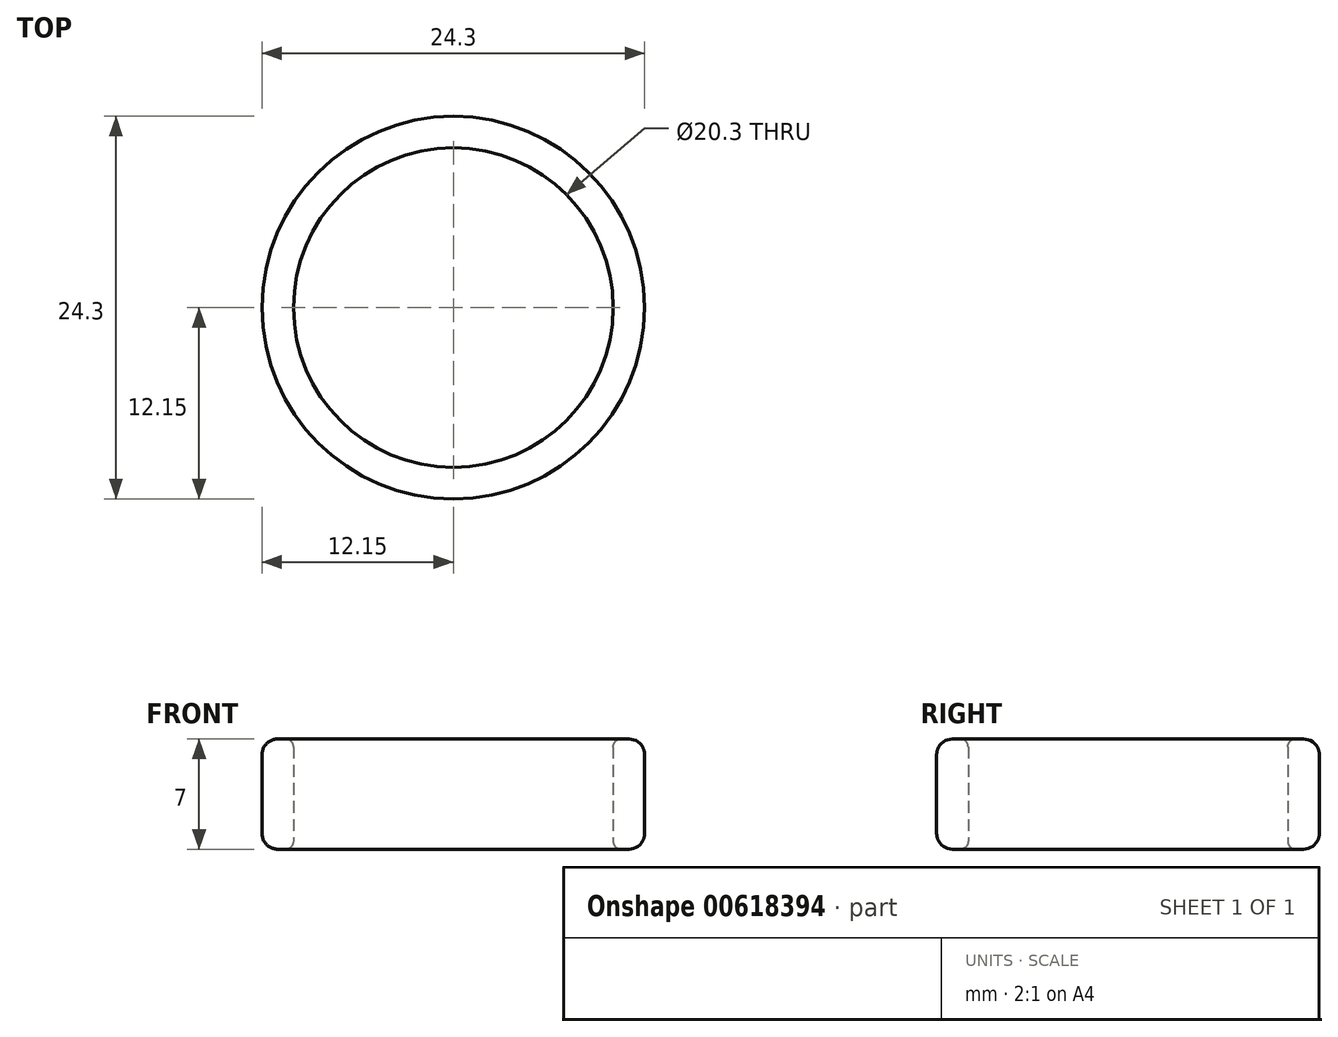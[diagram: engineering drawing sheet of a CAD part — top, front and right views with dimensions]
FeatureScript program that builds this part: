
annotation { "Feature Type Name" : "Feature", "Feature Type Description" : "" }
export const myFeature = defineFeature(function(context is Context, id is Id, definition is map)
    precondition{}
    {
        {
            var Q0;
            Q0=qCreatedBy(makeId("Front.planeOp"),FACE);
            var sketch = newSketch(context, id + "F0", { "sketchPlane" : qUnion([Q0])});
            skLineSegment(sketch, "E0", {"start": v(0, 0) * mm, "end": v(10.15, 0) * mm, "construction": true});
            skLineSegment(sketch, "E1.top", {"start": v(10.65, 3.5) * mm, "end": v(11.15, 3.5) * mm});
            skLineSegment(sketch, "E1.left", {"start": v(10.15, 0) * mm, "end": v(10.15, 3) * mm});
            skLineSegment(sketch, "E1.right", {"start": v(12.15, 0) * mm, "end": v(12.15, 2.5) * mm});
            skPoint(sketch, "E2.visualSharp", {"position": v(12.15, 3.5) * mm});
            skArc(sketch, "E2.filletArc", {"start": v(12.15, 2.5) * mm, "mid": v(11.86, 3.2) * mm, "end": v(11.15, 3.5) * mm});
            skPoint(sketch, "E3.visualSharp", {"position": v(10.15, 3.5) * mm});
            skArc(sketch, "E3.filletArc", {"start": v(10.65, 3.5) * mm, "mid": v(10.3, 3.35) * mm, "end": v(10.15, 3) * mm});
            skLineSegment(sketch, "E4.MirrorCS", {"start": v(10.65, -3.5) * mm, "end": v(11.15, -3.5) * mm});
            skArc(sketch, "E5.MirrorCS", {"start": v(10.65, -3.5) * mm, "mid": v(10.3, -3.35) * mm, "end": v(10.15, -3) * mm});
            skPoint(sketch, "E6.MirrorP", {"position": v(12.15, -3.5) * mm});
            skLineSegment(sketch, "E7.MirrorCS", {"start": v(10.15, 0) * mm, "end": v(10.15, -3) * mm});
            skArc(sketch, "E8.MirrorCS", {"start": v(12.15, -2.5) * mm, "mid": v(11.86, -3.2) * mm, "end": v(11.15, -3.5) * mm});
            skPoint(sketch, "E9.MirrorP", {"position": v(10.15, -3.5) * mm});
            skLineSegment(sketch, "E10.MirrorCS", {"start": v(12.15, 0) * mm, "end": v(12.15, -2.5) * mm});
            skPoint(sketch, "E11.MirrorCS.end.orphan", {"position": v(12.15, 0) * mm});
            skLineSegment(sketch, "E12", {"start": v(0, 0) * mm, "end": v(0, 5.63) * mm, "construction": true});
            skSolve(sketch);
        }
        {
            var Q0;
            Q0=makeQuery(id+"F0.imprint","IMPRINT",FACE,{"disambiguationData":[TD([[makeQuery(id+"F0.imprint","IMPRINT",EDGE,{"derivedFrom":sQuery(id+"F0.wireOp",EDGE,"E1.top")}),-1.0]])]});
            var Q1;
            Q1=sQuery(id+"F0.wireOp",EDGE,"E12");
            revolve(context, id + "F1", {"entities" : qUnion([Q0]), "axis" : qUnion([Q1]), "revolveType" : RevolveType.FULL});
        }
    });
